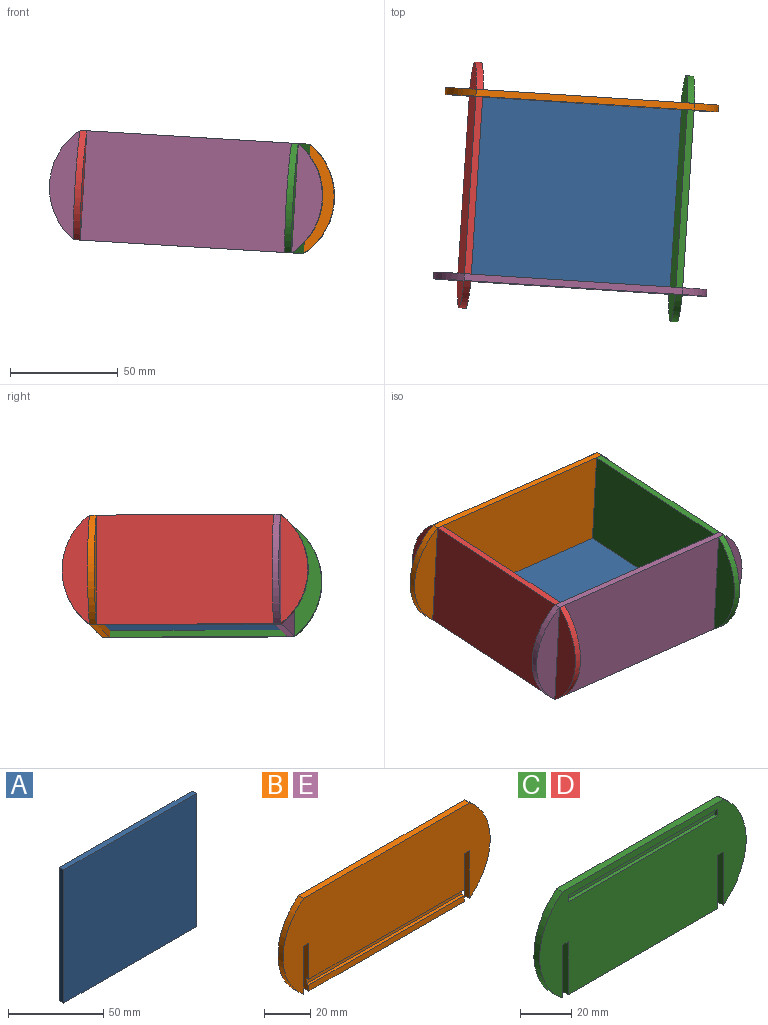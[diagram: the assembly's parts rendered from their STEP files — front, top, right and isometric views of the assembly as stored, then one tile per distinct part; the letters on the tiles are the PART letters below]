
ASSEMBLY  parts=5 mates=6
PART A: 6 faces, bbox 98.4x3.2x85.7 mm
  f0: plane 98.43x3.18mm, normal (0,0,1), area 312.5mm2, adj f1,f3,f4,f5
  f1: plane 85.73x3.18mm, normal (-1,0,0), area 272.2mm2, adj f0,f2,f4,f5
  f2: plane 98.43x3.18mm, normal (0,0,-1), area 312.5mm2, adj f1,f3,f4,f5
  f3: plane 85.73x3.18mm, normal (1,0,0), area 272.2mm2, adj f0,f2,f4,f5
  f4: plane 98.43x85.73mm, normal (0,-1,0), area 8437.5mm2, adj f0,f1,f2,f3
  f5: plane 98.43x85.73mm, normal (0,1,0), area 8437.5mm2, adj f0,f1,f2,f3
PART B: 16 faces, bbox 127x3.2x50.8 mm
  f0: plane 3.18x3.18mm, normal (0,0,-1), area 10.1mm2, adj f1,f9,f10,f11
  f1: plane 25.4x3.18mm, normal (-1,0,0), area 75.6mm2, adj f0,f2,f10,f11,f12,f13,f14,f15
  f2: plane 95.25x1.59mm, normal (0,0,-1), area 151.2mm2, adj f1,f3,f10,f15
  f3: plane 25.4x3.18mm, normal (1,0,0), area 75.6mm2, adj f2,f4,f10,f11,f12,f13,f14,f15
  f4: plane 3.18x3.18mm, normal (0,0,-1), area 10.1mm2, adj f3,f5,f10,f11
  f5: plane 25.4x3.18mm, normal (-1,0,0), area 80.6mm2, adj f4,f6,f10,f11
  f6: cylinder r=31.75mm len=50.8mm, axis (0,1,0), area 187mm2, adj f5,f7,f10,f11
  f7: plane 101.6x3.18mm, normal (0,0,1), area 322.6mm2, adj f6,f8,f10,f11
  f8: cylinder r=31.75mm len=50.8mm, axis (0,1,0), area 187mm2, adj f7,f9,f10,f11
  f9: plane 25.4x3.18mm, normal (1,0,0), area 80.6mm2, adj f0,f8,f10,f11
  f10: plane 127x50.8mm, normal (0,-1,0), area 5297mm2, adj f0,f1,f2,f3,f4,f5,f6,f7
  f11: plane 127x50.8mm, normal (0,1,0), area 5901.8mm2, adj f0,f1,f3,f4,f5,f6,f7,f8
  f12: plane 95.25x1.59mm, normal (0,0,1), area 151.2mm2, adj f1,f3,f14,f15
  f13: plane 95.25x3.18mm, normal (0,0,-1), area 302.4mm2, adj f1,f3,f11,f14
  f14: plane 95.25x3.18mm, normal (0,-1,0), area 302.4mm2, adj f1,f3,f12,f13
  f15: plane 95.25x3.18mm, normal (0,-1,0), area 302.4mm2, adj f1,f2,f3,f12
PART C: 17 faces, bbox 114.3x3.2x50.8 mm
  f0: plane 3.18x1.59mm, normal (1,0,0), area 5mm2, adj f1,f13,f14,f16
  f1: plane 82.55x1.59mm, normal (0,0,-1), area 131mm2, adj f0,f2,f14,f16
  f2: plane 3.18x1.59mm, normal (-1,0,0), area 5mm2, adj f1,f13,f14,f16
  f3: plane 25.4x3.18mm, normal (1,0,0), area 80.6mm2, adj f4,f12,f14,f15
  f4: plane 3.18x3.18mm, normal (0,0,-1), area 10.1mm2, adj f3,f5,f14,f15
  f5: plane 25.4x3.18mm, normal (-1,0,0), area 80.6mm2, adj f4,f6,f14,f15
  f6: cylinder r=31.75mm len=50.8mm, axis (0,1,0), area 187mm2, adj f5,f7,f14,f15
  f7: plane 88.9x3.18mm, normal (0,0,1), area 282.3mm2, adj f6,f8,f14,f15
  f8: cylinder r=31.75mm len=50.8mm, axis (0,1,0), area 187mm2, adj f7,f9,f14,f15
  f9: plane 25.4x3.18mm, normal (1,0,0), area 80.6mm2, adj f8,f10,f14,f15
  f10: plane 3.18x3.18mm, normal (0,0,-1), area 10.1mm2, adj f9,f11,f14,f15
  f11: plane 25.4x3.18mm, normal (-1,0,0), area 80.6mm2, adj f10,f12,f14,f15
  f12: plane 82.55x3.18mm, normal (0,0,-1), area 262.1mm2, adj f3,f11,f14,f15
  f13: plane 82.55x1.59mm, normal (0,0,1), area 131mm2, adj f0,f2,f14,f16
  f14: plane 114.3x50.8mm, normal (0,-1,0), area 4994.5mm2, adj f0,f1,f2,f3,f4,f5,f6,f7
  f15: plane 114.3x50.8mm, normal (0,1,0), area 5256.6mm2, adj f3,f4,f5,f6,f7,f8,f9,f10
  f16: plane 82.55x3.18mm, normal (0,-1,0), area 262.1mm2, adj f0,f1,f2,f13
PART D: same geometry as C
PART E: same geometry as B
PLACE A rot(axis=(0,-0.71,0.71),174.9deg) t=(155.27,-3.34,-119.94)mm
PLACE B rot(axis=(-0.02,0.69,-0.73),5.1deg) t=(-26.37,116.47,-112.11)mm
PLACE C rot(axis=(-0.73,-0.68,0.02),177.6deg) t=(68.26,60.12,-173.71)mm
PLACE D rot(axis=(0.68,-0.73,-0.02),177.5deg) t=(-32.24,77.58,-167.62)mm fixed
PLACE E rot(axis=(0.03,0,1),176.3deg) t=(69.14,21.24,-117.9)mm
MATE fastened E.f0 <-> C.f10  axis (-0.06,0,-1) through (69.2,22.92,-92.46)mm
MATE fastened A.f0 <-> E.f15  axis (-0.06,-1,0) through (18.93,26.08,-110.09)mm
MATE fastened D.f10 <-> B.f0  axis (0.06,0,1) through (-23.36,114.78,-86.85)mm
MATE fastened D.f4 <-> E.f4  axis (0.06,0,1) through (-28.85,29.23,-86.52)mm
MATE fastened C.f4 <-> B.f4  axis (0.06,0,1) through (74.68,108.47,-92.79)mm
MATE fastened A.f3 <-> D.f16  axis (-1,0.06,0.06) through (-27.35,72.01,-107.28)mm
